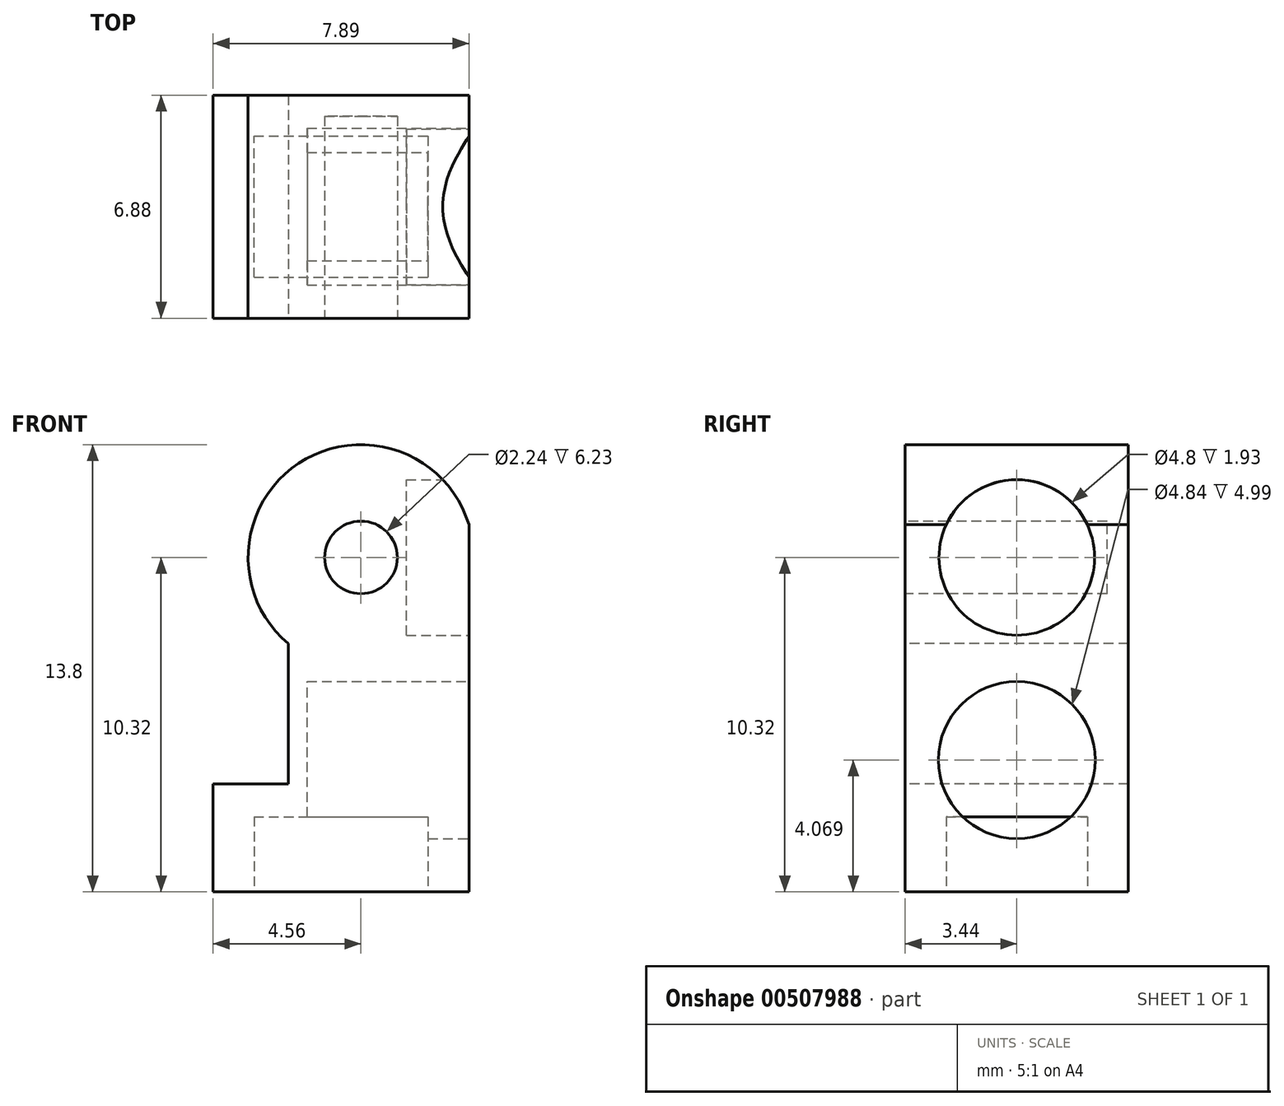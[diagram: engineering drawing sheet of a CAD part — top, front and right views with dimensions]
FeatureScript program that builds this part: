
annotation { "Feature Type Name" : "Feature", "Feature Type Description" : "" }
export const myFeature = defineFeature(function(context is Context, id is Id, definition is map)
    precondition{}
    {
        {
            var Q0;
            Q0=qCreatedBy(makeId("Front.planeOp"),FACE);
            var sketch = newSketch(context, id + "F0", { "sketchPlane" : qUnion([Q0])});
            skCircle(sketch, "E0", {"center": v(0, 0) * mm, "radius": 3.48 * mm});
            skSolve(sketch);
        }
        {
            var Q0;
            Q0 = qSketchRegion(id + "F0", true);
            var Q1;
            Q1 = qSketchRegion(id + "F2", true);
            extrude(context, id + "F1", {"entities" : qUnion([Q0, Q1]), "depth" : 6.88 * mm, "offsetDistance" : 25 * mm});
        }
        {
            var Q0;
            Q0=makeQuery(id+"F1.opExtrude","CAP_FACE",FACE,{"disambiguationData":[OSD([sQuery(id+"F0.wireOp",EDGE,"E0")])],"isStart":false});
            var sketch = newSketch(context, id + "F2", { "sketchPlane" : qUnion([Q0])});
            skCircle(sketch, "E1", {"center": v(0, 0) * mm, "radius": 1.12 * mm});
            skSolve(sketch);
        }
        {
            var Q0;
            Q0 = qSketchRegion(id + "F2", true);
            extrude(context, id + "F3", {"entities" : qUnion([Q0]), "operationType" : NewBodyOperationType.REMOVE, "oppositeDirection" : true, "depth" : 6.23 * mm, "offsetDistance" : 25 * mm});
        }
        {
            var Q0;
            Q0=makeQuery(id+"F1.opExtrude","CAP_FACE",FACE,{"disambiguationData":[OSD([sQuery(id+"F0.wireOp",EDGE,"E0")])],"isStart":false});
            var sketch = newSketch(context, id + "F4", { "sketchPlane" : qUnion([Q0])});
            skLineSegment(sketch, "E2", {"start": v(3.33, 4.37) * mm, "end": v(3.33, -5.86) * mm});
            skLineSegment(sketch, "E3", {"start": v(3.33, 4.37) * mm, "end": v(7.09, -1.44) * mm});
            skLineSegment(sketch, "E4", {"start": v(7.09, -1.44) * mm, "end": v(3.33, -5.86) * mm});
            skSolve(sketch);
        }
        {
            var Q0;
            Q0 = qSketchRegion(id + "F4", true);
            extrude(context, id + "F5", {"entities" : qUnion([Q0]), "operationType" : NewBodyOperationType.REMOVE, "oppositeDirection" : true, "depth" : 25 * mm, "offsetDistance" : 25 * mm});
        }
        {
            var Q0;
            Q0=makeQuery(id+"F1.opExtrude","CAP_FACE",FACE,{"disambiguationData":[OSD([sQuery(id+"F0.wireOp",EDGE,"E0")])],"isStart":false});
            var sketch = newSketch(context, id + "F6", { "sketchPlane" : qUnion([Q0])});
            skLineSegment(sketch, "E5", {"start": v(3.33, -1.01) * mm, "end": v(3.33, -10.32) * mm});
            skLineSegment(sketch, "E6", {"start": v(3.33, -10.32) * mm, "end": v(-4.56, -10.32) * mm});
            skLineSegment(sketch, "E7", {"start": v(-4.56, -10.32) * mm, "end": v(-4.56, -7) * mm});
            skLineSegment(sketch, "E8", {"start": v(-4.56, -7) * mm, "end": v(-2.24, -7) * mm});
            skLineSegment(sketch, "E9", {"start": v(-2.24, -7) * mm, "end": v(-2.24, -2.66) * mm});
            skArc(sketch, "E10", {"start": v(-2.24, -2.66) * mm, "mid": v(0.88, -2.97) * mm, "end": v(3.33, -1.01) * mm});
            skSolve(sketch);
        }
        {
            var Q0;
            Q0 = qSketchRegion(id + "F6", true);
            extrude(context, id + "F7", {"entities" : qUnion([Q0]), "operationType" : NewBodyOperationType.ADD, "oppositeDirection" : true, "depth" : 6.88 * mm, "offsetDistance" : 25 * mm});
        }
        {
            var Q0;
            Q0=makeQuery(id+"F7.opExtrude","SWEPT_FACE",FACE,{"disambiguationData":[OSD([sQuery(id+"F6.wireOp",EDGE,"E6")])]});
            var sketch = newSketch(context, id + "F8", { "sketchPlane" : qUnion([Q0])});
            skLineSegment(sketch, "E11", {"start": v(2.07, 1.26) * mm, "end": v(2.07, 5.62) * mm});
            skLineSegment(sketch, "E12", {"start": v(-3.3, 5.62) * mm, "end": v(-3.3, 1.26) * mm});
            skLineSegment(sketch, "E13", {"start": v(-3.3, 5.62) * mm, "end": v(2.07, 5.62) * mm});
            skLineSegment(sketch, "E14", {"start": v(-3.3, 1.26) * mm, "end": v(2.07, 1.26) * mm});
            skSolve(sketch);
        }
        {
            var Q0;
            Q0 = qSketchRegion(id + "F8", true);
            extrude(context, id + "F9", {"entities" : qUnion([Q0]), "operationType" : NewBodyOperationType.REMOVE, "oppositeDirection" : true, "depth" : 2.32 * mm, "offsetDistance" : 25 * mm});
        }
        {
            var Q0;
            Q0=makeQuery(id+"F7.boolean.opBoolean","MERGE",FACE,{"derivedFrom":[makeQuery(id+"F5.boolean.opBoolean","COPY",FACE,{"derivedFrom":makeQuery(id+"F5.opExtrude","SWEPT_FACE",FACE,{"disambiguationData":[OSD([sQuery(id+"F4.wireOp",EDGE,"E2")])]})}),makeQuery(id+"F7.opExtrude","SWEPT_FACE",FACE,{"disambiguationData":[OSD([sQuery(id+"F6.wireOp",EDGE,"E5")])]})]});
            var sketch = newSketch(context, id + "F10", { "sketchPlane" : qUnion([Q0])});
            skCircle(sketch, "E15", {"center": v(-3.44, 0) * mm, "radius": 2.4 * mm});
            skPoint(sketch, "E15.centerSnap0", {"position": v(-3.44, 1.01) * mm});
            skSolve(sketch);
        }
        {
            var Q0;
            Q0 = qSketchRegion(id + "F10", true);
            extrude(context, id + "F11", {"entities" : qUnion([Q0]), "operationType" : NewBodyOperationType.REMOVE, "oppositeDirection" : true, "depth" : 1.93 * mm, "offsetDistance" : 25 * mm});
        }
        {
            var Q0;
            Q0=makeQuery(id+"F7.boolean.opBoolean","MERGE",FACE,{"derivedFrom":[makeQuery(id+"F5.boolean.opBoolean","COPY",FACE,{"derivedFrom":makeQuery(id+"F5.opExtrude","SWEPT_FACE",FACE,{"disambiguationData":[OSD([sQuery(id+"F4.wireOp",EDGE,"E2")])]})}),makeQuery(id+"F7.opExtrude","SWEPT_FACE",FACE,{"disambiguationData":[OSD([sQuery(id+"F6.wireOp",EDGE,"E5")])]})]});
            var sketch = newSketch(context, id + "F12", { "sketchPlane" : qUnion([Q0])});
            skCircle(sketch, "E16", {"center": v(-3.44, -6.25) * mm, "radius": 2.42 * mm});
            skPoint(sketch, "E16.centerSnap0", {"position": v(-3.44, -10.32) * mm});
            skSolve(sketch);
        }
        {
            var Q0;
            Q0 = qSketchRegion(id + "F12", true);
            extrude(context, id + "F13", {"entities" : qUnion([Q0]), "operationType" : NewBodyOperationType.REMOVE, "oppositeDirection" : true, "depth" : 5 * mm, "offsetDistance" : 25 * mm});
        }
    });
